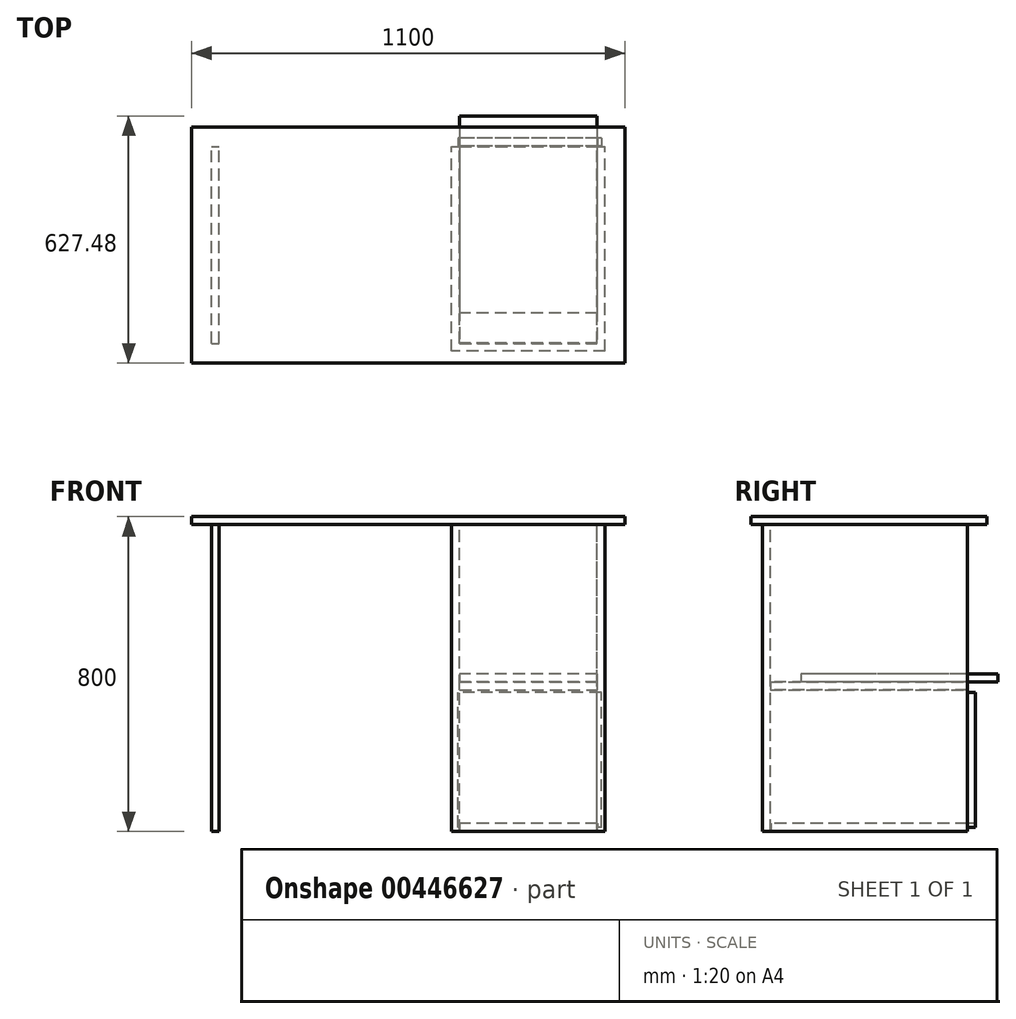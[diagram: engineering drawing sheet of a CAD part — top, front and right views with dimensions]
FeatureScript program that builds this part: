
annotation { "Feature Type Name" : "Feature", "Feature Type Description" : "" }
export const myFeature = defineFeature(function(context is Context, id is Id, definition is map)
    precondition{}
    {
        {
            var Q0;
            Q0=qCreatedBy(makeId("Top.planeOp"),FACE);
            var sketch = newSketch(context, id + "F0", { "sketchPlane" : qUnion([Q0])});
            skLineSegment(sketch, "E0.bottom", {"start": v(-542.94, 344.07) * mm, "end": v(557.06, 344.07) * mm});
            skLineSegment(sketch, "E0.top", {"start": v(-542.94, -255.93) * mm, "end": v(557.06, -255.93) * mm});
            skLineSegment(sketch, "E0.left", {"start": v(-542.94, 344.07) * mm, "end": v(-542.94, -255.93) * mm});
            skLineSegment(sketch, "E0.right", {"start": v(557.06, 344.07) * mm, "end": v(557.06, -255.93) * mm});
            skSolve(sketch);
        }
        {
            var Q0;
            Q0=makeQuery(id+"F0.imprint","IMPRINT",FACE,{"disambiguationData":[TD([[makeQuery(id+"F0.imprint","IMPRINT",EDGE,{"derivedFrom":sQuery(id+"F0.wireOp",EDGE,"E0.bottom")}),-1.0]])]});
            extrude(context, id + "F1", {"entities" : qUnion([Q0]), "depth" : 20 * mm});
        }
        {
            var Q0;
            Q0=makeQuery(id+"F1.opExtrude","CAP_FACE",FACE,{"disambiguationData":[OSD([sQuery(id+"F0.wireOp",EDGE,"E0.bottom"),sQuery(id+"F0.wireOp",EDGE,"E0.top"),sQuery(id+"F0.wireOp",EDGE,"E0.left"),sQuery(id+"F0.wireOp",EDGE,"E0.right")])],"isStart":true});
            var sketch = newSketch(context, id + "F2", { "sketchPlane" : qUnion([Q0])});
            skLineSegment(sketch, "E1.bottom", {"start": v(-492.94, 205.93) * mm, "end": v(-472.94, 205.93) * mm});
            skLineSegment(sketch, "E1.top", {"start": v(-492.94, -294.07) * mm, "end": v(-472.94, -294.07) * mm});
            skLineSegment(sketch, "E1.left", {"start": v(-492.94, 205.93) * mm, "end": v(-492.94, -294.07) * mm});
            skLineSegment(sketch, "E1.right", {"start": v(-472.94, 205.93) * mm, "end": v(-472.94, -294.07) * mm});
            skLineSegment(sketch, "E2.bottom", {"start": v(487.06, 205.93) * mm, "end": v(507.06, 205.93) * mm});
            skLineSegment(sketch, "E2.top", {"start": v(487.06, -294.07) * mm, "end": v(507.06, -294.07) * mm});
            skLineSegment(sketch, "E2.left", {"start": v(487.06, 205.93) * mm, "end": v(487.06, -294.07) * mm});
            skLineSegment(sketch, "E2.right", {"start": v(507.06, 205.93) * mm, "end": v(507.06, -294.07) * mm});
            skLineSegment(sketch, "E3.bottom", {"start": v(117.06, 205.93) * mm, "end": v(137.06, 205.93) * mm});
            skLineSegment(sketch, "E3.top", {"start": v(117.06, -294.07) * mm, "end": v(137.06, -294.07) * mm});
            skLineSegment(sketch, "E3.left", {"start": v(117.06, 205.93) * mm, "end": v(117.06, -294.07) * mm});
            skLineSegment(sketch, "E3.right", {"start": v(137.06, 205.93) * mm, "end": v(137.06, -294.07) * mm});
            skSolve(sketch);
        }
        {
            var Q0;
            Q0 = qSketchRegion(id + "F2", true);
            extrude(context, id + "F3", {"entities" : qUnion([Q0]), "operationType" : NewBodyOperationType.ADD, "depth" : 780 * mm});
        }
        {
            var Q0;
            Q0=makeQuery(id+"F3.opExtrude","SWEPT_FACE",FACE,{"disambiguationData":[OSD([sQuery(id+"F2.wireOp",EDGE,"E2.bottom")])]});
            var sketch = newSketch(context, id + "F4", { "sketchPlane" : qUnion([Q0])});
            skLineSegment(sketch, "E4.bottom", {"start": v(507.06, -780) * mm, "end": v(117.06, -780) * mm});
            skLineSegment(sketch, "E4.top", {"start": v(507.06, 0) * mm, "end": v(117.06, 0) * mm});
            skLineSegment(sketch, "E4.left", {"start": v(507.06, -780) * mm, "end": v(507.06, 0) * mm});
            skLineSegment(sketch, "E4.right", {"start": v(117.06, -780) * mm, "end": v(117.06, 0) * mm});
            skSolve(sketch);
        }
        {
            var Q0;
            Q0 = qSketchRegion(id + "F4", true);
            extrude(context, id + "F5", {"entities" : qUnion([Q0]), "operationType" : NewBodyOperationType.ADD, "depth" : 20 * mm});
        }
        {
            var Q0;
            Q0=qCreatedBy(makeId("Top.planeOp"),FACE);
            cPlane(context, id + "F6", {"entities" : qUnion([Q0]), "cplaneType" : CPlaneType.OFFSET, "offset" : 400 * mm, "oppositeDirection" : true, "width" : 150 * mm, "height" : 150 * mm});
        }
        {
            var Q0;
            Q0=qCreatedBy(id+"F6.planeOp",FACE);
            var sketch = newSketch(context, id + "F7", { "sketchPlane" : qUnion([Q0])});
            skLineSegment(sketch, "E5.bottom", {"start": v(137.29, -205.7) * mm, "end": v(487.29, -205.7) * mm});
            skLineSegment(sketch, "E5.top", {"start": v(137.29, 294.3) * mm, "end": v(487.29, 294.3) * mm});
            skLineSegment(sketch, "E5.left", {"start": v(137.29, -205.7) * mm, "end": v(137.29, 294.3) * mm});
            skLineSegment(sketch, "E5.right", {"start": v(487.29, -205.7) * mm, "end": v(487.29, 294.3) * mm});
            skSolve(sketch);
        }
        {
            var Q0;
            Q0 = qSketchRegion(id + "F7", true);
            extrude(context, id + "F8", {"entities" : qUnion([Q0]), "operationType" : NewBodyOperationType.ADD, "oppositeDirection" : true, "depth" : 20 * mm});
        }
        {
            var Q0;
            Q0=qCreatedBy(makeId("Top.planeOp"),FACE);
            cPlane(context, id + "F9", {"entities" : qUnion([Q0]), "cplaneType" : CPlaneType.OFFSET, "offset" : 780 * mm, "oppositeDirection" : true, "width" : 150 * mm, "height" : 150 * mm});
        }
        {
            var Q0;
            Q0=qCreatedBy(id+"F6.planeOp",FACE);
            var sketch = newSketch(context, id + "F10", { "sketchPlane" : qUnion([Q0])});
            skLineSegment(sketch, "E6.bottom", {"start": v(487.06, 371.55) * mm, "end": v(137.06, 371.55) * mm});
            skLineSegment(sketch, "E6.top", {"start": v(487.06, -128.23) * mm, "end": v(137.06, -128.23) * mm});
            skLineSegment(sketch, "E6.left", {"start": v(487.06, 371.55) * mm, "end": v(487.06, -128.45) * mm});
            skLineSegment(sketch, "E6.right", {"start": v(137.06, 371.55) * mm, "end": v(137.06, -128.23) * mm});
            skSolve(sketch);
        }
        {
            var Q0;
            {var subQ0=sQuery(id+"F10.wireOp",EDGE,"E6.bottom");Q0=makeQuery(id+"F10.imprint","IMPRINT",FACE,{"disambiguationData":[TD([[makeQuery(id+"F10.imprint","IMPRINT",EDGE,{"derivedFrom":subQ0}),1.0]])]});}
            extrude(context, id + "F11", {"entities" : qUnion([Q0]), "depth" : 20 * mm});
        }
        {
            var Q0;
            Q0=qCreatedBy(id+"F9.planeOp",FACE);
            var sketch = newSketch(context, id + "F12", { "sketchPlane" : qUnion([Q0])});
            skLineSegment(sketch, "E7.bottom", {"start": v(487.86, 295.18) * mm, "end": v(137.86, 295.18) * mm});
            skLineSegment(sketch, "E7.top", {"start": v(487.86, -204.82) * mm, "end": v(137.86, -204.82) * mm});
            skLineSegment(sketch, "E7.left", {"start": v(487.86, 295.18) * mm, "end": v(487.86, -204.82) * mm});
            skLineSegment(sketch, "E7.right", {"start": v(137.86, 295.18) * mm, "end": v(137.86, -204.82) * mm});
            skSolve(sketch);
        }
        {
            var Q0;
            Q0=makeQuery(id+"F12.imprint","IMPRINT",FACE,{"disambiguationData":[TD([[makeQuery(id+"F12.imprint","IMPRINT",EDGE,{"derivedFrom":sQuery(id+"F12.wireOp",EDGE,"E7.bottom")}),1.0]])]});
            extrude(context, id + "F13", {"entities" : qUnion([Q0]), "operationType" : NewBodyOperationType.ADD, "depth" : 20 * mm});
        }
        {
            var Q0;
            Q0=makeQuery(id+"F13.opExtrude","SWEPT_FACE",FACE,{"disambiguationData":[OSD([sQuery(id+"F12.wireOp",EDGE,"E7.bottom")])]});
            var sketch = newSketch(context, id + "F14", { "sketchPlane" : qUnion([Q0])});
            skLineSegment(sketch, "E8.bottom", {"start": v(-497.62, -769.5) * mm, "end": v(-133.07, -769.5) * mm});
            skLineSegment(sketch, "E8.top", {"start": v(-497.62, -426.81) * mm, "end": v(-133.07, -426.81) * mm});
            skLineSegment(sketch, "E8.left", {"start": v(-497.62, -769.5) * mm, "end": v(-497.62, -426.81) * mm});
            skLineSegment(sketch, "E8.right", {"start": v(-133.07, -769.5) * mm, "end": v(-133.07, -426.81) * mm});
            skSolve(sketch);
        }
        {
            var Q0;
            Q0=makeQuery(id+"F14.imprint","IMPRINT",FACE,{"disambiguationData":[TD([[makeQuery(id+"F14.imprint","IMPRINT",EDGE,{"derivedFrom":sQuery(id+"F14.wireOp",EDGE,"E8.top")}),-1.0]])]});
            extrude(context, id + "F15", {"entities" : qUnion([Q0]), "depth" : 20 * mm});
        }
    });
